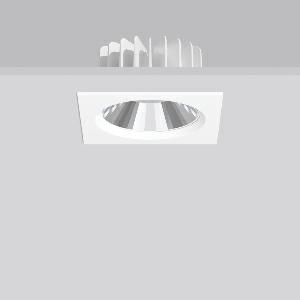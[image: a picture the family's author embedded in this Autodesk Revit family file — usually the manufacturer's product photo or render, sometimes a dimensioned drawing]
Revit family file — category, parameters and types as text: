
# Revit family: ledona_square_ip20_901796_002_76_cc92
name_source: partatom
category: Lighting Fixtures
units: mm (PartAtom-declared; Revit-internal decimal feet)

## family parameters
Cut with Voids When Loaded = No
Host = Face
Light Source = No
Part Type = Normal
Room Calculation Point = No
Round Connector Dimension = Use Diameter
Shared = No

## types (1)
- MultiLumen 1 (1 x LED Modul 930, 1650 lm, 3000)
    Apparent Load = 12 VA
    Approval mark = CE
    CIE Flux Codes = 91 100 100 100 100
    Color Rendering = 90
    Color Temperature = 3000
    Default Elevation = 1800 mm
    Description = Series: LEDONA square
Recessed LED downlight featuring advanced technology and sophisticated design. Housing: die-cast aluminium constructed as heat sink. Square cover plate: die-cast aluminium, powder coated. Round ceiling cut-out also with square types. MultiLumen: Luminous flux adjustable in different steps. Best colour rendering index Ra>90. Installation without tools thanks to spring fastening system. Connected converter included in separate gearbox. With connecting cable (L 250 mm). Suitable for through wiring as standard. 
Colour: white
Length: 170 mm
Width: 170 mm
Height: 3 mm
Cut-out diameter: 160 mm
Recess height: 89 mm
Luminaire: recess height: 89 mm
Lamp: LED
Socket: without socket
Colour temperature: 3000K
Colour rendering index (CRI): 92
System power: 12 W
Rated luminous flux: 1650 lm
Luminous efficiency: 138 lm/W
System power 2: 19 W
Rated luminous flux 2: 2550 lm
Luminous efficiency 2: 134 lm/W
System power 3: 27 W
Rated luminous flux 3: 3450 lm
Luminous efficiency 3: 128 lm/W
System power 4: 39 W
Rated luminous flux 4: 4600 lm
Luminous efficiency 4: 118 lm/W
Control gear: Converter, dimmable, DALI
Protection class: II
Type of protection: IP 20
    Height = 0 mm  [stored 0 ft]
    Lamp = 1 x LED Modul 930
    Lamp Light Flux = 1650 lm
    Lamp count = 1
    Length = 170 mm  [stored 0.557743 ft]
    Lifetime = 50000 h
    Luminous efficacy = 138 lm/W
    Manufacturer = RZB
    ModVariant = No
    Model = 901796.002.76
    Mounting Place = Ceiling
    Mounting Type = Recessed
    Number of Poles = 1
    OnlyDefault = Yes
    Power Factor = 1
    Product Name = LEDONA square IP20
    Product group = Recessed downlights
    ProductGroupID = 402
    Protection Class = Protection class II
    Protection Degree = IP 20
    RLX_Detail_Level = 1
    RLX_Emergency_Light_Flux = 0 lm
    RLX_Emergency_Type = 0
    RLX_Emergency_Type_DB = No
    RlxData = <blob elided: 33541 chars, md5=995df97a>
    Socket = socket
    Standby Power = 0 W
    System Light Flux = 1650 lm
    System Power = 12 W
    Type Comments = MultiLumen 1
    Type Image = 901391.002.jpg
    URL = http://relux.com
    VarID = multilumen_1
    Voltage = 230 V
    Voltage Range = 220-240 V
    Weight = 0.00 kg
    Width = 170 mm  [stored 0.557743 ft]

note: [stored X ft] marks values corroborated as IEEE doubles in the binary element streams (Revit-internal decimal feet)

## geometry (parser evidence)
native form markers: Blend x4, Sweep x9
no freeform markers — native parametric forms only
